# Revit family: Toilet-Wall_Mount-KOHLER-Veil-K-31539IN.rfa_
name_source: partatom
category: Plumbing Fixtures
units: mm (PartAtom-declared; Revit-internal decimal feet)

## family parameters
Cut with Voids When Loaded = No
Host = Face
Maintain Annotation Orientation = No
OmniClass Number = 23.31.19.00
OmniClass Title = Toilets
Part Type = Normal
Room Calculation Point = No
Round Connector Dimension = Use Diameter
Shared = No

## types (3) — shared parameters
ADA Compliant = No
Assembly Code = D2010100
CW Connection = Yes
Cold Water Inlet = Cold Water Inlet
Date Modified = 06/13/2024
Description = Wall Hung Elongated Bowl
Flow Rate = 0 GPM
HW Connection = No
Height = 384 mm
Hot Water Inlet = Hot Water Inlet
Length = 553 mm
Manufacturer = Kohler Co.
Master Format 2014 = 22 42 13.13
Master Format 2014 Name = Residential Water Closets
Material = Vitreous China
Pressure = 0.00 psi
Product Name = Veil
Seat Included = No
URL = https://www.kohler.co.in
Vent Connection = No
Waste Connection = Yes
Waste Water Outlet = Waste Water Outlet
WaterSense Certified = No
Width = 385 mm
zero-valued in all types: Default Elevation

## per-type parameters (varying)
| type | Finish | Flush Rate- GPF | Flush Rate- LPF | Model | Secondary Finish | Type |
| 4 LPF, DGS-Indigo | KOHLER-Vitreous_China-DGS-Indigo | 1.056 LPF | 4 LPF | K-31539IN-DGS | KOHLER-Plastic-DGS-Indigo | 1 |
| 4 LPF, 7-Black Black | Kohler-Vitreous_China-7-Black_Black | 1.056 LPF | 4 LPF | K-31539IN-7 | Kohler-Plastic-7-Black_Black | 2 |
| 6 LPF, 0-White | Kohler-Vitreous_China-0-White | 1.585 LPF | 6 LPF | K-31539IN-SS-0 | Kohler-Plastic-0-White | 3 |

## geometry (parser evidence)
native form markers: Sweep x6
no freeform markers — native parametric forms only
